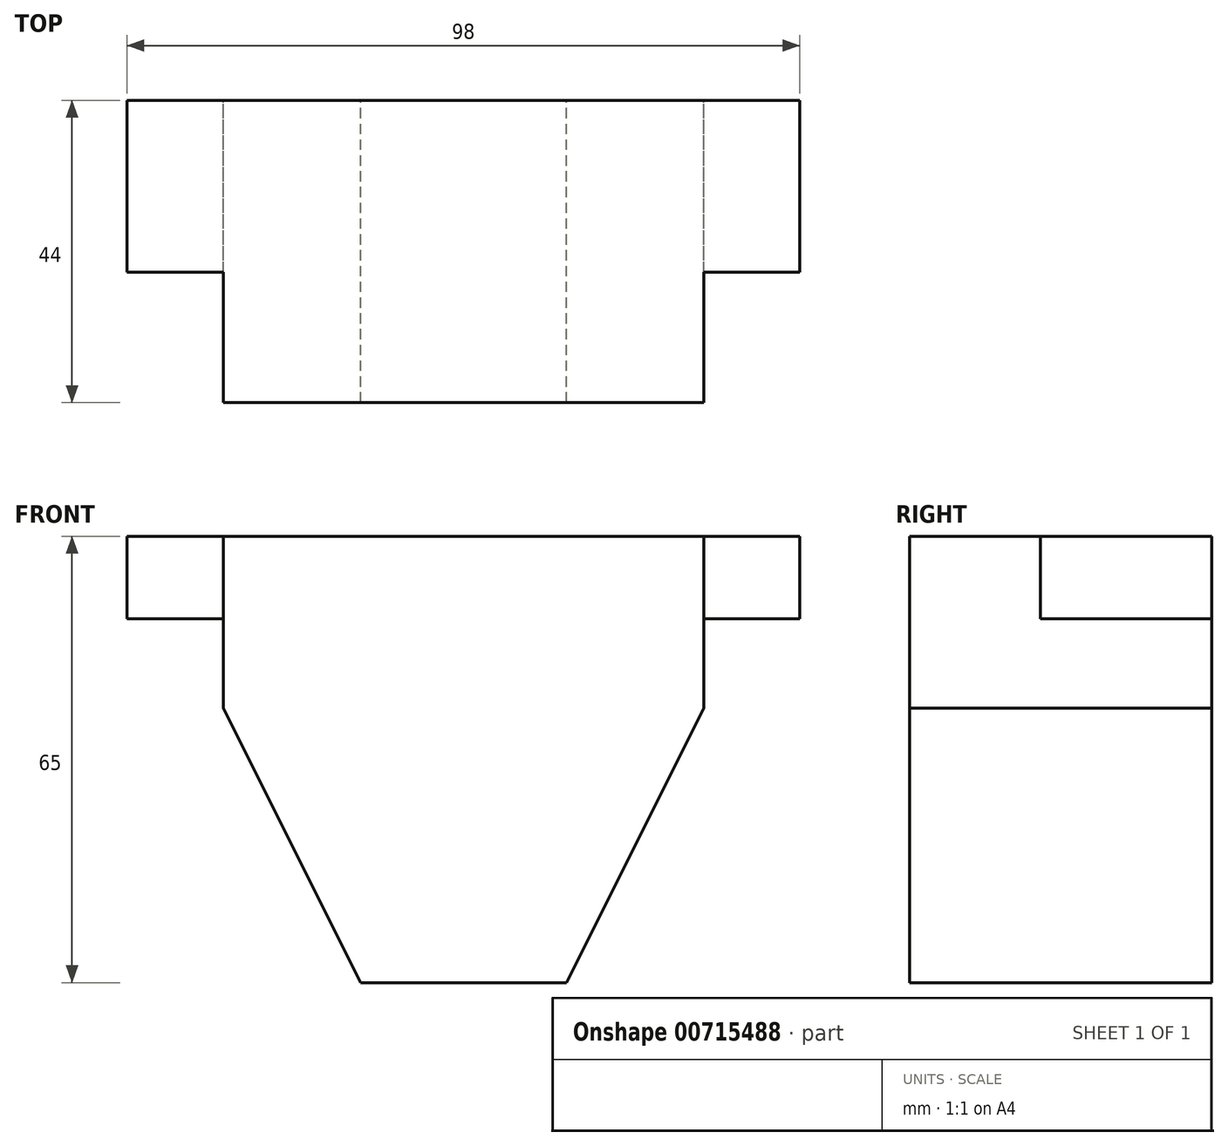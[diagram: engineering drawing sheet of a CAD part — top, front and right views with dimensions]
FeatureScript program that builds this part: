
annotation { "Feature Type Name" : "Feature", "Feature Type Description" : "" }
export const myFeature = defineFeature(function(context is Context, id is Id, definition is map)
    precondition{}
    {
        {
            var Q0;
            Q0=qCreatedBy(makeId("Front.planeOp"),FACE);
            var sketch = newSketch(context, id + "F0", { "sketchPlane" : qUnion([Q0])});
            skLineSegment(sketch, "E0", {"start": v(-49, 23.64) * mm, "end": v(-49, 11.64) * mm});
            skLineSegment(sketch, "E1", {"start": v(-49, 11.64) * mm, "end": v(-35, 11.64) * mm});
            skLineSegment(sketch, "E2", {"start": v(-35, 11.64) * mm, "end": v(-35, -1.36) * mm});
            skLineSegment(sketch, "E3", {"start": v(-35, -1.36) * mm, "end": v(-15, -41.36) * mm});
            skLineSegment(sketch, "E4", {"start": v(-15, -41.36) * mm, "end": v(15, -41.36) * mm});
            skLineSegment(sketch, "E5", {"start": v(15, -41.36) * mm, "end": v(35, -1.36) * mm});
            skLineSegment(sketch, "E6", {"start": v(35, -1.36) * mm, "end": v(35, 11.64) * mm});
            skLineSegment(sketch, "E7", {"start": v(35, 11.64) * mm, "end": v(49, 11.64) * mm});
            skLineSegment(sketch, "E8", {"start": v(49, 11.64) * mm, "end": v(49, 23.64) * mm});
            skLineSegment(sketch, "E9", {"start": v(-49, 23.64) * mm, "end": v(49, 23.64) * mm});
            skSolve(sketch);
        }
        {
            var Q0;
            Q0 = qSketchRegion(id + "F0", true);
            extrude(context, id + "F1", {"entities" : qUnion([Q0]), "depth" : 44 * mm, "offsetDistance" : 25 * mm});
        }
        {
            var Q0;
            Q0=makeQuery(id+"F1.opExtrude","SWEPT_FACE",FACE,{"disambiguationData":[OSD([sQuery(id+"F0.wireOp",EDGE,"E9")])]});
            var sketch = newSketch(context, id + "F2", { "sketchPlane" : qUnion([Q0])});
            skLineSegment(sketch, "E10.bottom", {"start": v(49, -44) * mm, "end": v(35, -44) * mm});
            skLineSegment(sketch, "E10.top", {"start": v(49, -25) * mm, "end": v(35, -25) * mm});
            skLineSegment(sketch, "E10.left", {"start": v(49, -44) * mm, "end": v(49, -25) * mm});
            skLineSegment(sketch, "E10.right", {"start": v(35, -44) * mm, "end": v(35, -25) * mm});
            skLineSegment(sketch, "E11.bottom", {"start": v(-49, -44) * mm, "end": v(-35, -44) * mm});
            skLineSegment(sketch, "E11.top", {"start": v(-49, -25) * mm, "end": v(-35, -25) * mm});
            skLineSegment(sketch, "E11.left", {"start": v(-49, -44) * mm, "end": v(-49, -25) * mm});
            skLineSegment(sketch, "E11.right", {"start": v(-35, -44) * mm, "end": v(-35, -25) * mm});
            skSolve(sketch);
        }
        {
            var Q0;
            Q0 = qSketchRegion(id + "F2", true);
            extrude(context, id + "F3", {"entities" : qUnion([Q0]), "operationType" : NewBodyOperationType.REMOVE, "endBound" : BoundingType.THROUGH_ALL, "oppositeDirection" : true, "depth" : 25 * mm, "offsetDistance" : 25 * mm});
        }
    });
